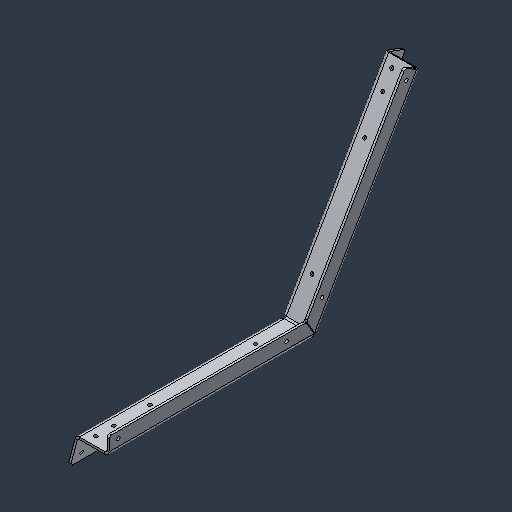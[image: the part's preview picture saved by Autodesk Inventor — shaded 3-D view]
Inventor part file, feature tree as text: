
AUTODESK INVENTOR PART (.ipt)
format: ipt  version: 2024.3 (Build 283343000, 343)  size: 166,400 bytes
history: native  units: mm (DEFAULTED — no unit token found)
features: mirror x1
ambient origin geometry x8: Origin, YZ Plane, XZ Plane, XY Plane, X Axis, Y Axis, Z Axis, Center Point
bodies: Solid1 (feature_tree)
feature tree (1):
  mirror  "Mirror1"
